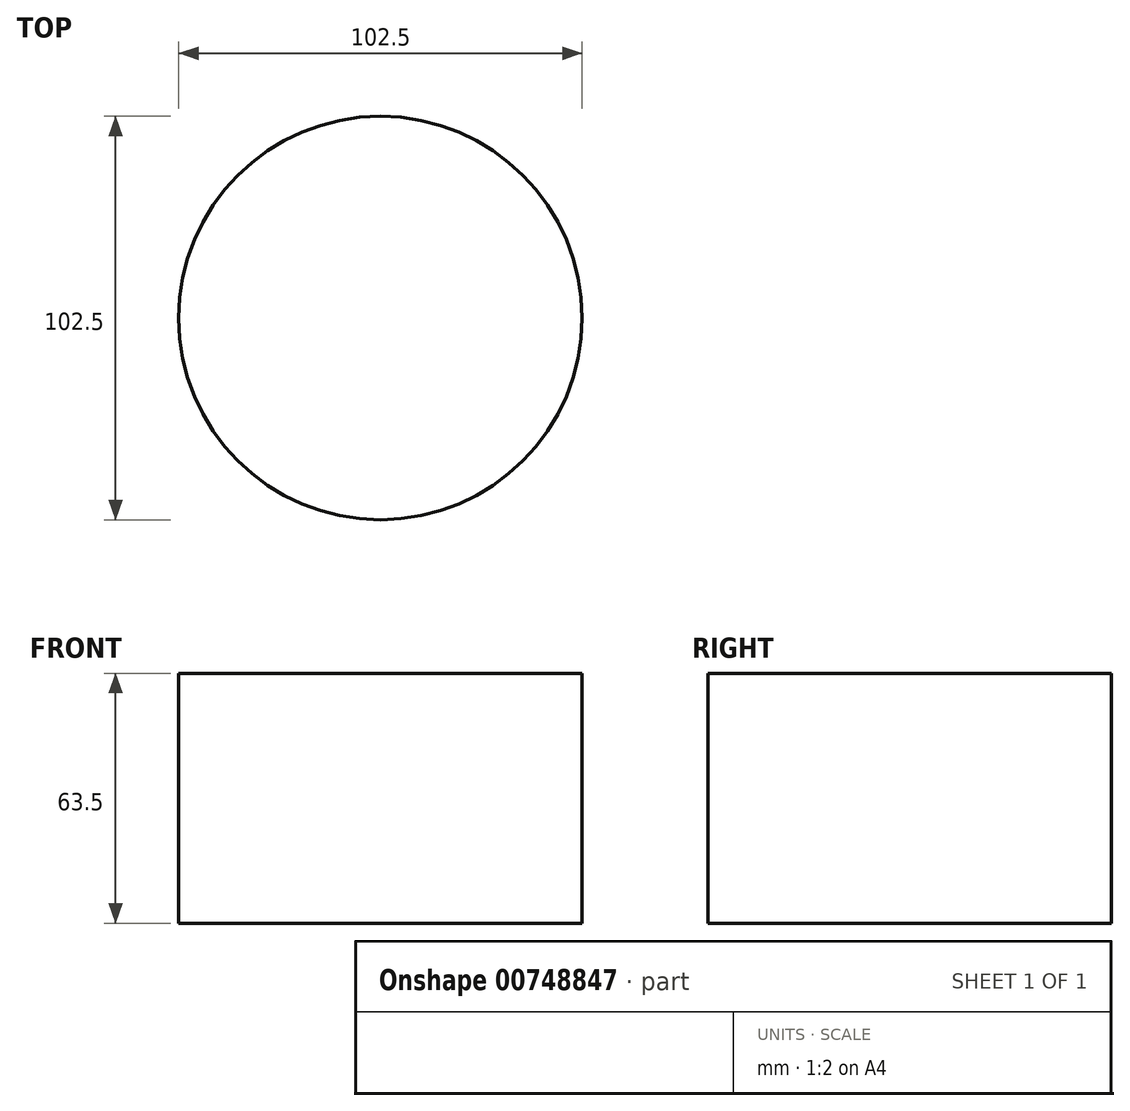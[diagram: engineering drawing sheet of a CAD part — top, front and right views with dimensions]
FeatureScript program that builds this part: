
annotation { "Feature Type Name" : "Feature", "Feature Type Description" : "" }
export const myFeature = defineFeature(function(context is Context, id is Id, definition is map)
    precondition{}
    {
        {
            var Q0;
            Q0=qCreatedBy(makeId("Top.planeOp"),FACE);
            var sketch = newSketch(context, id + "F0", { "sketchPlane" : qUnion([Q0])});
            skCircle(sketch, "E0", {"center": v(0, 0) * mm, "radius": 51.25 * mm});
            skSolve(sketch);
        }
        {
            var Q0;
            Q0 = qSketchRegion(id + "F0", true);
            var Q1;
            Q1=makeQuery(id+"F0.imprint","IMPRINT",FACE,{"disambiguationData":[TD([[makeQuery(id+"F0.imprint","IMPRINT",EDGE,{"derivedFrom":sQuery(id+"F0.wireOp",EDGE,"E0")}),1.0]])]});
            extrude(context, id + "F1", {"entities" : qUnion([Q0, Q1]), "depth" : 63.5 * mm, "offsetDistance" : 25.4 * mm});
        }
    });
